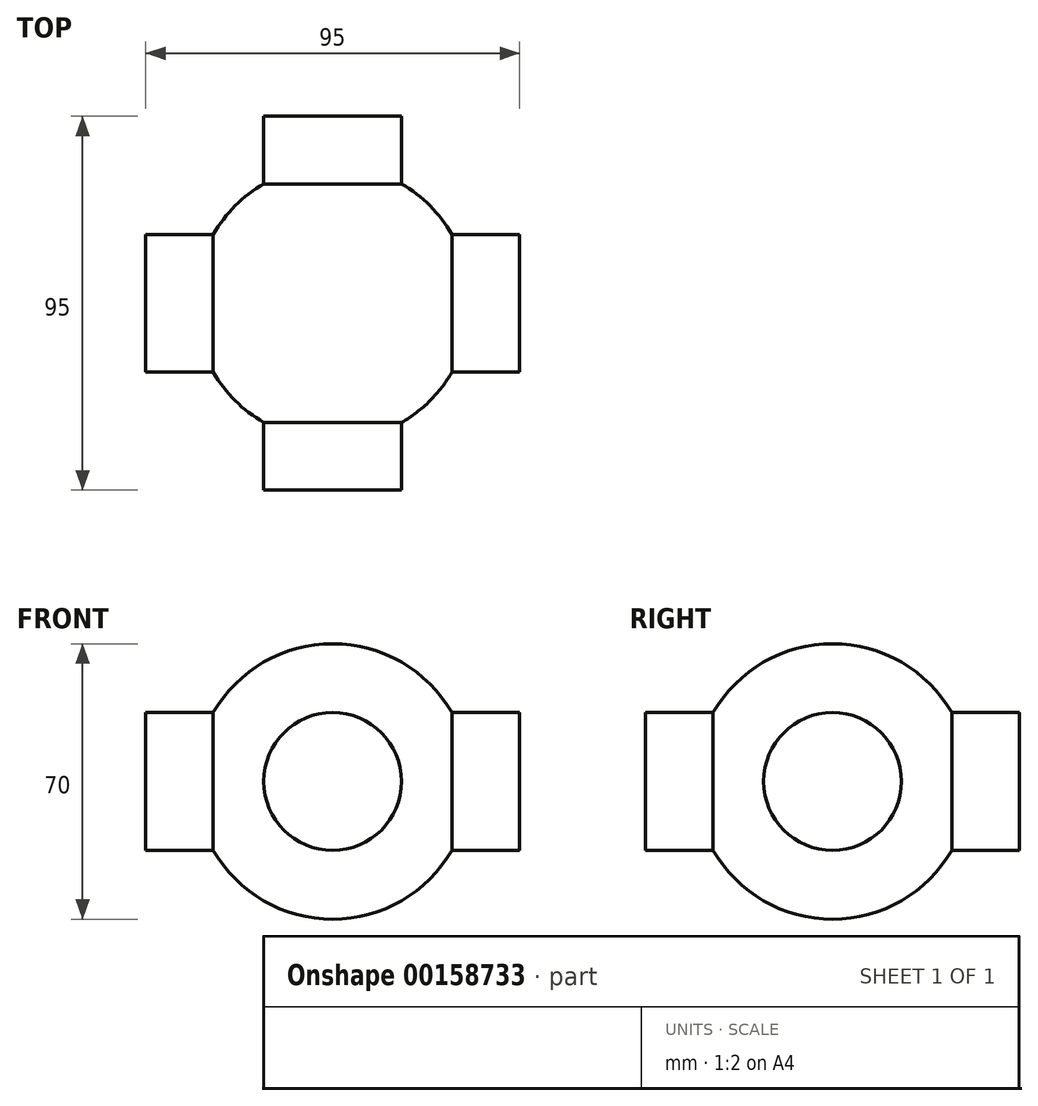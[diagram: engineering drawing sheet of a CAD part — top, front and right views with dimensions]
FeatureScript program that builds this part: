
annotation { "Feature Type Name" : "Feature", "Feature Type Description" : "" }
export const myFeature = defineFeature(function(context is Context, id is Id, definition is map)
    precondition{}
    {
        {
            var Q0;
            Q0=qCreatedBy(makeId("Front.planeOp"),FACE);
            var sketch = newSketch(context, id + "F0", { "sketchPlane" : qUnion([Q0])});
            skArc(sketch, "E0", {"start": v(0, 35) * mm, "mid": v(-35, 0) * mm, "end": v(0, -35) * mm});
            skLineSegment(sketch, "E1", {"start": v(0, 35) * mm, "end": v(0, -35) * mm});
            skSolve(sketch);
        }
        {
            var Q0;
            Q0 = qSketchRegion(id + "F0", true);
            var Q1;
            Q1=sQuery(id+"F0.wireOp",EDGE,"E1");
            revolve(context, id + "F1", {"entities" : qUnion([Q0]), "axis" : qUnion([Q1]), "revolveType" : RevolveType.FULL});
        }
        {
            var Q0;
            Q0=qCreatedBy(makeId("Front.planeOp"),FACE);
            var sketch = newSketch(context, id + "F2", { "sketchPlane" : qUnion([Q0])});
            skCircle(sketch, "E2", {"center": v(0, 0) * mm, "radius": 17.5 * mm});
            skSolve(sketch);
        }
        {
            var Q0;
            Q0 = qSketchRegion(id + "F2", true);
            extrude(context, id + "F3", {"entities" : qUnion([Q0]), "operationType" : NewBodyOperationType.ADD, "endBound" : BoundingType.SYMMETRIC, "depth" : 95 * mm});
        }
        {
            var Q0;
            Q0=qCreatedBy(makeId("Right.planeOp"),FACE);
            var sketch = newSketch(context, id + "F4", { "sketchPlane" : qUnion([Q0])});
            skCircle(sketch, "E3", {"center": v(0, 0) * mm, "radius": 17.5 * mm});
            skSolve(sketch);
        }
        {
            var Q0;
            Q0 = qSketchRegion(id + "F4", true);
            extrude(context, id + "F5", {"entities" : qUnion([Q0]), "operationType" : NewBodyOperationType.ADD, "endBound" : BoundingType.SYMMETRIC, "depth" : 95 * mm});
        }
    });
